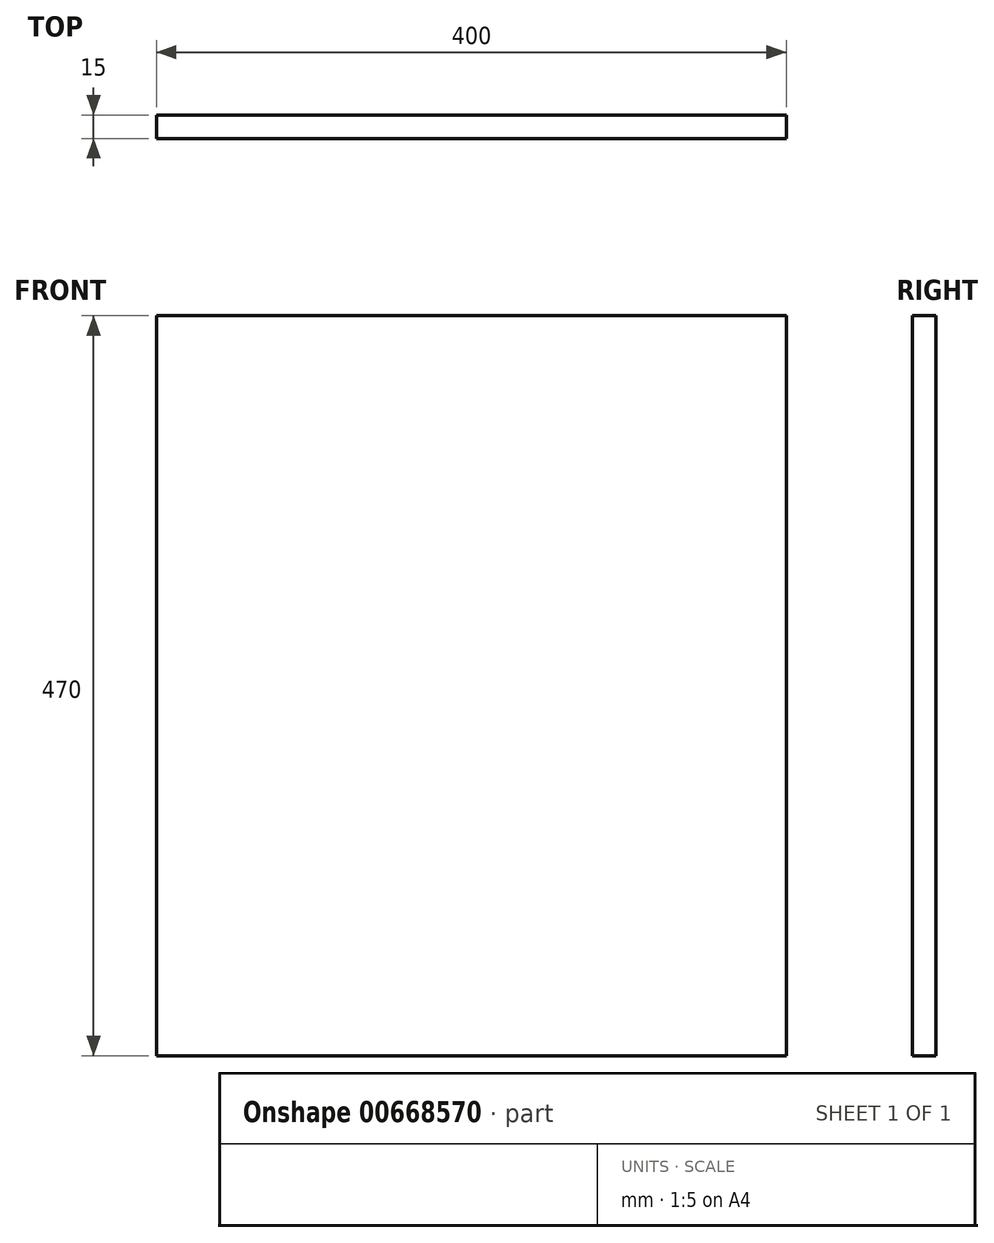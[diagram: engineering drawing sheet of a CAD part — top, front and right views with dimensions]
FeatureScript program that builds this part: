
annotation { "Feature Type Name" : "Feature", "Feature Type Description" : "" }
export const myFeature = defineFeature(function(context is Context, id is Id, definition is map)
    precondition{}
    {
        {
            var Q0;
            Q0=qCreatedBy(makeId("Front.planeOp"),FACE);
            var sketch = newSketch(context, id + "F0", { "sketchPlane" : qUnion([Q0])});
            skLineSegment(sketch, "E0.bottom", {"start": v(0, 0) * mm, "end": v(400, 0) * mm});
            skLineSegment(sketch, "E0.top", {"start": v(0, 470) * mm, "end": v(400, 470) * mm});
            skLineSegment(sketch, "E0.left", {"start": v(0, 0) * mm, "end": v(0, 470) * mm});
            skLineSegment(sketch, "E0.right", {"start": v(400, 0) * mm, "end": v(400, 470) * mm});
            skSolve(sketch);
        }
        {
            var Q0;
            Q0=makeQuery(id+"F0.imprint","IMPRINT",FACE,{"disambiguationData":[TD([[makeQuery(id+"F0.imprint","IMPRINT",EDGE,{"derivedFrom":sQuery(id+"F0.wireOp",EDGE,"E0.bottom")}),1.0]])]});
            extrude(context, id + "F1", {"entities" : qUnion([Q0]), "depth" : 15 * mm, "offsetDistance" : 25 * mm});
        }
    });
